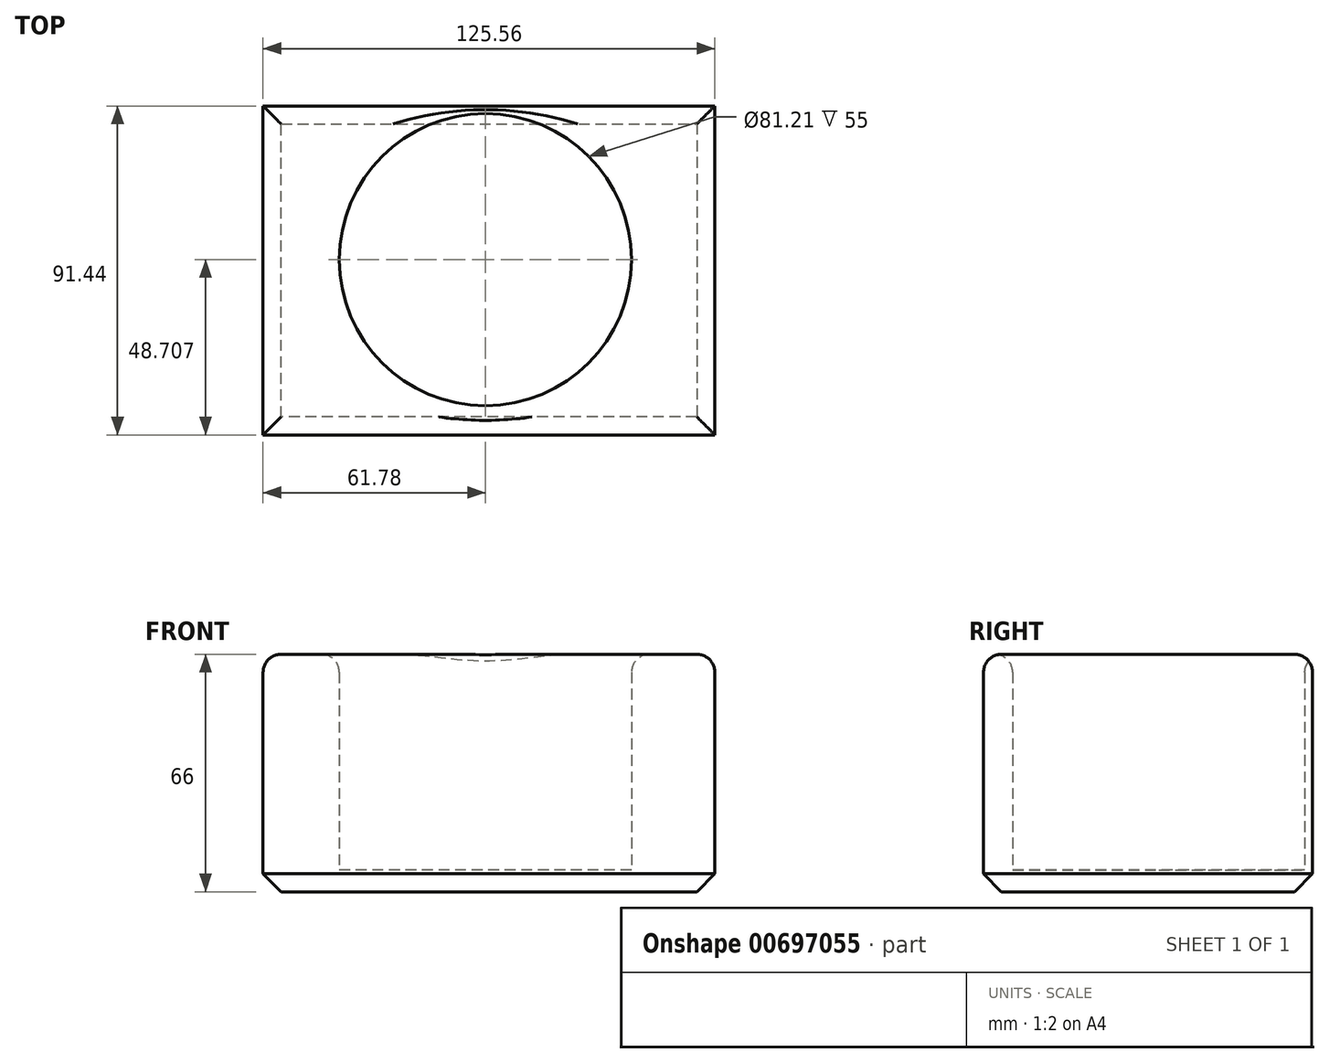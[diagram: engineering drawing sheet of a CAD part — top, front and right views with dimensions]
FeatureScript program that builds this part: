
annotation { "Feature Type Name" : "Feature", "Feature Type Description" : "" }
export const myFeature = defineFeature(function(context is Context, id is Id, definition is map)
    precondition{}
    {
        {
            var Q0;
            Q0=qCreatedBy(makeId("Top.planeOp"),FACE);
            var sketch = newSketch(context, id + "F0", { "sketchPlane" : qUnion([Q0])});
            skLineSegment(sketch, "E0.bottom", {"start": v(63.78, 37.12) * mm, "end": v(-61.78, 37.12) * mm});
            skLineSegment(sketch, "E0.top", {"start": v(63.78, -54.32) * mm, "end": v(-61.78, -54.32) * mm});
            skLineSegment(sketch, "E0.left", {"start": v(63.78, 37.12) * mm, "end": v(63.78, -54.32) * mm});
            skLineSegment(sketch, "E0.right", {"start": v(-61.78, 37.12) * mm, "end": v(-61.78, -54.32) * mm});
            skCircle(sketch, "E1", {"center": v(0, -5.61) * mm, "radius": 40.6 * mm});
            skSolve(sketch);
        }
        {
            var Q0;
            Q0 = qSketchRegion(id + "F0", true);
            extrude(context, id + "F1", {"entities" : qUnion([Q0]), "depth" : 60 * mm, "offsetDistance" : 25 * mm});
        }
        {
            var Q0;
            Q0=makeQuery(id+"F1.opExtrude","CAP_FACE",FACE,{"disambiguationData":[OSD([sQuery(id+"F0.wireOp",EDGE,"E0.bottom"),sQuery(id+"F0.wireOp",EDGE,"E0.top"),sQuery(id+"F0.wireOp",EDGE,"E0.left"),sQuery(id+"F0.wireOp",EDGE,"E0.right"),sQuery(id+"F0.wireOp",EDGE,"E1")])],"isStart":true});
            var sketch = newSketch(context, id + "F2", { "sketchPlane" : qUnion([Q0])});
            skLineSegment(sketch, "E2.bottom", {"start": v(63.78, 54.32) * mm, "end": v(-61.78, 54.32) * mm});
            skLineSegment(sketch, "E2.top", {"start": v(63.78, -37.12) * mm, "end": v(-61.78, -37.12) * mm});
            skLineSegment(sketch, "E2.left", {"start": v(63.78, 54.32) * mm, "end": v(63.78, -37.12) * mm});
            skLineSegment(sketch, "E2.right", {"start": v(-61.78, 54.32) * mm, "end": v(-61.78, -37.12) * mm});
            skLineSegment(sketch, "E3.bottom", {"start": v(59.69, 50.39) * mm, "end": v(-58.6, 50.39) * mm});
            skLineSegment(sketch, "E3.top", {"start": v(59.69, -37.12) * mm, "end": v(-58.6, -37.12) * mm});
            skLineSegment(sketch, "E3.left", {"start": v(59.69, 50.39) * mm, "end": v(59.69, -37.12) * mm});
            skLineSegment(sketch, "E3.right", {"start": v(-58.6, 50.39) * mm, "end": v(-58.6, -37.12) * mm});
            skSolve(sketch);
        }
        {
            var Q0;
            Q0 = qSketchRegion(id + "F2", true);
            extrude(context, id + "F3", {"entities" : qUnion([Q0]), "operationType" : NewBodyOperationType.ADD, "depth" : 6 * mm, "offsetDistance" : 25 * mm});
        }
        {
            var Q0;
            Q0=makeQuery(id+"F1.opExtrude","CAP_EDGE",EDGE,{"disambiguationData":[OSD([sQuery(id+"F0.wireOp",EDGE,"E0.bottom")])],"isStart":false});
            var Q1;
            Q1=makeQuery(id+"F1.opExtrude","CAP_FACE",FACE,{"disambiguationData":[OSD([sQuery(id+"F0.wireOp",EDGE,"E0.bottom"),sQuery(id+"F0.wireOp",EDGE,"E0.top"),sQuery(id+"F0.wireOp",EDGE,"E0.left"),sQuery(id+"F0.wireOp",EDGE,"E0.right"),sQuery(id+"F0.wireOp",EDGE,"E1")])],"isStart":false});
            fillet(context, id + "F4", {"entities" : qUnion([Q0, Q1]), "radius" : 5 * mm, "tangentPropagation" : true, "allowEdgeOverflow" : false});
        }
        {
            var Q0;
            Q0=makeQuery(id+"F3.opExtrude","CAP_EDGE",EDGE,{"disambiguationData":[OSD([sQuery(id+"F2.wireOp",EDGE,"E2.top"),sQuery(id+"F2.wireOp",EDGE,"E3.top")])],"isStart":false});
            var Q1;
            Q1=makeQuery(id+"F3.opExtrude","CAP_FACE",FACE,{"disambiguationData":[OSD([sQuery(id+"F2.wireOp",EDGE,"E2.bottom"),sQuery(id+"F2.wireOp",EDGE,"E2.top"),sQuery(id+"F2.wireOp",EDGE,"E2.left"),sQuery(id+"F2.wireOp",EDGE,"E2.right"),sQuery(id+"F2.wireOp",EDGE,"E3.top")])],"isStart":false});
            chamfer(context, id + "F5", {"entities" : qUnion([Q0, Q1]), "width" : 5 * mm, "tangentPropagation" : true});
        }
    });
